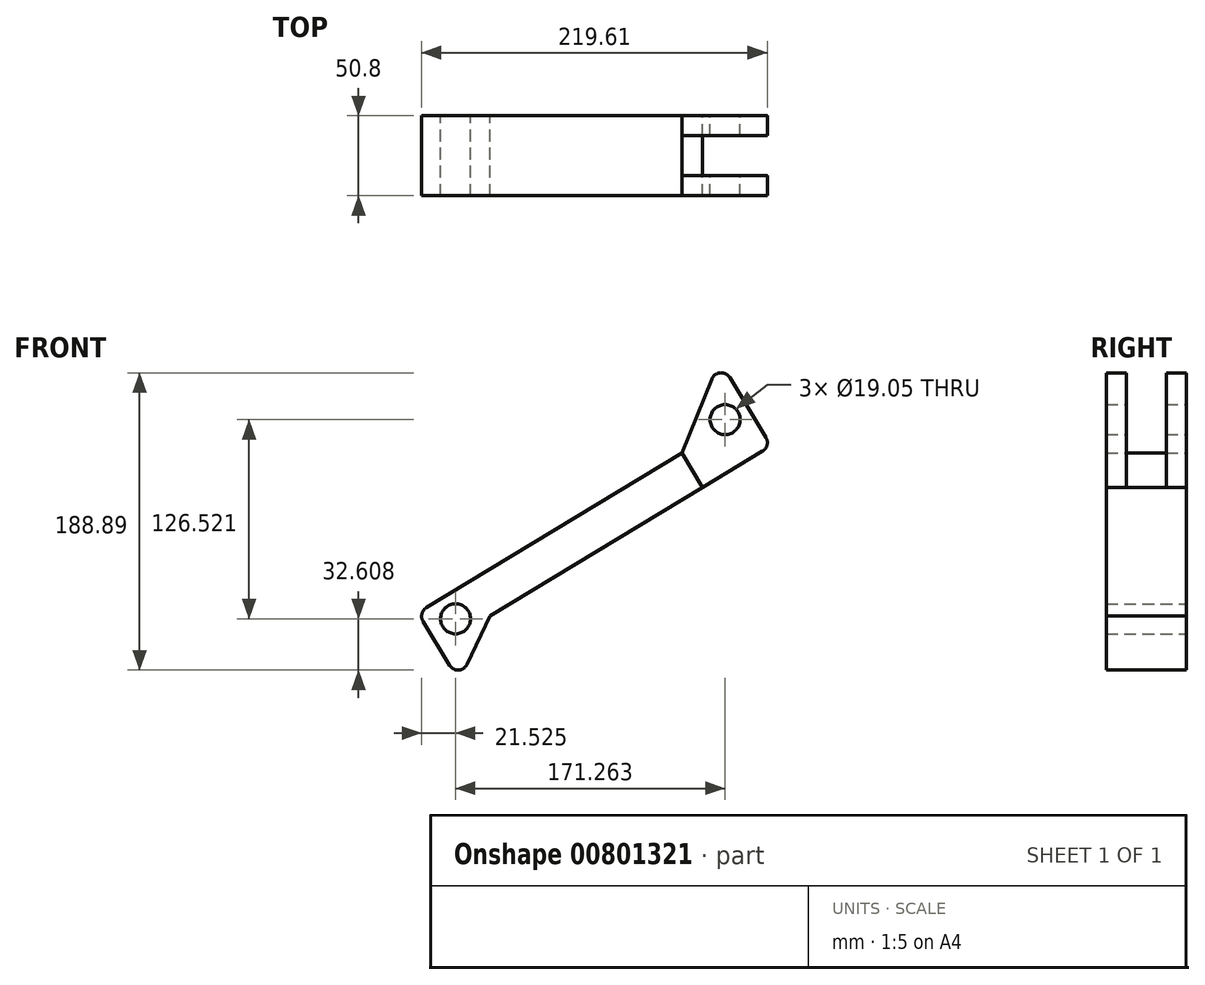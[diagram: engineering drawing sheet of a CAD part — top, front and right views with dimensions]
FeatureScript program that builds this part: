
annotation { "Feature Type Name" : "Feature", "Feature Type Description" : "" }
export const myFeature = defineFeature(function(context is Context, id is Id, definition is map)
    precondition{}
    {
        {
            var Q0;
            Q0=qCreatedBy(makeId("Front.planeOp"),FACE);
            var sketch = newSketch(context, id + "F0", { "sketchPlane" : qUnion([Q0])});
            skLineSegment(sketch, "E0", {"start": v(61.2, 59.5) * mm, "end": v(-73.94, -22.2) * mm});
            skLineSegment(sketch, "E1.0", {"start": v(74.34, 37.77) * mm, "end": v(-60.8, -43.94) * mm});
            skLineSegment(sketch, "E2", {"start": v(-73.94, -22.2) * mm, "end": v(-60.8, -43.94) * mm});
            skLineSegment(sketch, "E3", {"start": v(61.2, 59.5) * mm, "end": v(74.34, 37.77) * mm});
            skLineSegment(sketch, "E4", {"start": v(74.34, 37.77) * mm, "end": v(112.37, 60.76) * mm});
            skLineSegment(sketch, "E5", {"start": v(114.52, 69.48) * mm, "end": v(91.52, 107.52) * mm});
            skLineSegment(sketch, "E6", {"start": v(80.2, 106.61) * mm, "end": v(61.2, 59.5) * mm});
            skPoint(sketch, "E7.visualSharp", {"position": v(84.95, 118.39) * mm});
            skArc(sketch, "E7.filletArc", {"start": v(91.52, 107.52) * mm, "mid": v(85.58, 110.57) * mm, "end": v(80.2, 106.61) * mm});
            skPoint(sketch, "E8.visualSharp", {"position": v(117.8, 64.05) * mm});
            skArc(sketch, "E8.filletArc", {"start": v(112.37, 60.76) * mm, "mid": v(115.25, 64.68) * mm, "end": v(114.52, 69.48) * mm});
            skLineSegment(sketch, "E9", {"start": v(-73.94, -22.2) * mm, "end": v(-101.11, -38.63) * mm});
            skLineSegment(sketch, "E10", {"start": v(-103.26, -47.35) * mm, "end": v(-86.4, -75.23) * mm});
            skLineSegment(sketch, "E11", {"start": v(-75.22, -74.65) * mm, "end": v(-60.8, -43.94) * mm});
            skPoint(sketch, "E12.visualSharp", {"position": v(-80.26, -85.39) * mm});
            skArc(sketch, "E12.filletArc", {"start": v(-86.4, -75.23) * mm, "mid": v(-80.63, -78.29) * mm, "end": v(-75.22, -74.65) * mm});
            skPoint(sketch, "E13.visualSharp", {"position": v(-106.54, -41.91) * mm});
            skArc(sketch, "E13.filletArc", {"start": v(-101.11, -38.63) * mm, "mid": v(-104, -42.54) * mm, "end": v(-103.26, -47.35) * mm});
            skCircle(sketch, "E14", {"center": v(88.62, 80.83) * mm, "radius": 9.53 * mm});
            skPoint(sketch, "E15.startSnap0", {"position": v(-80.63, -78.29) * mm});
            skCircle(sketch, "E16", {"center": v(-82.65, -45.7) * mm, "radius": 9.53 * mm});
            skLineSegment(sketch, "E17.0", {"start": v(67.76, 48.63) * mm, "end": v(-67.37, -33.07) * mm, "construction": true});
            skSolve(sketch);
        }
        {
            var Q0;
            Q0=makeQuery(id+"F0.imprint","IMPRINT",FACE,{"disambiguationData":[TD([[makeQuery(id+"F0.imprint","IMPRINT",EDGE,{"derivedFrom":sQuery(id+"F0.wireOp",EDGE,"E5")}),1.0]])]});
            var Q1;
            Q1=makeQuery(id+"F0.imprint","IMPRINT",FACE,{"disambiguationData":[TD([[makeQuery(id+"F0.imprint","IMPRINT",EDGE,{"derivedFrom":sQuery(id+"F0.wireOp",EDGE,"E14")}),-1.0]])]});
            extrude(context, id + "F1", {"entities" : qUnion([Q0, Q1]), "endBound" : BoundingType.SYMMETRIC, "depth" : 50.8 * mm, "offsetDistance" : 25.4 * mm});
        }
        {
            var Q0;
            Q0=makeQuery(id+"F0.imprint","IMPRINT",FACE,{"disambiguationData":[TD([[makeQuery(id+"F0.imprint","IMPRINT",EDGE,{"derivedFrom":sQuery(id+"F0.wireOp",EDGE,"E0")}),1.0]])]});
            extrude(context, id + "F2", {"entities" : qUnion([Q0]), "endBound" : BoundingType.SYMMETRIC, "depth" : 50.8 * mm, "offsetDistance" : 25.4 * mm});
        }
        {
            var Q0;
            Q0=makeQuery(id+"F0.imprint","IMPRINT",FACE,{"disambiguationData":[TD([[makeQuery(id+"F0.imprint","IMPRINT",EDGE,{"derivedFrom":sQuery(id+"F0.wireOp",EDGE,"E3")}),1.0]])]});
            extrude(context, id + "F3", {"entities" : qUnion([Q0]), "operationType" : NewBodyOperationType.REMOVE, "endBound" : BoundingType.SYMMETRIC, "depth" : 25.4 * mm, "offsetDistance" : 25.4 * mm});
        }
        {
            var Q0;
            Q0=makeQuery(id+"F0.imprint","IMPRINT",FACE,{"disambiguationData":[TD([[makeQuery(id+"F0.imprint","IMPRINT",EDGE,{"derivedFrom":sQuery(id+"F0.wireOp",EDGE,"E2")}),-1.0]])]});
            extrude(context, id + "F4", {"entities" : qUnion([Q0]), "operationType" : NewBodyOperationType.ADD, "endBound" : BoundingType.SYMMETRIC, "depth" : 50.8 * mm, "offsetDistance" : 25.4 * mm});
        }
    });
